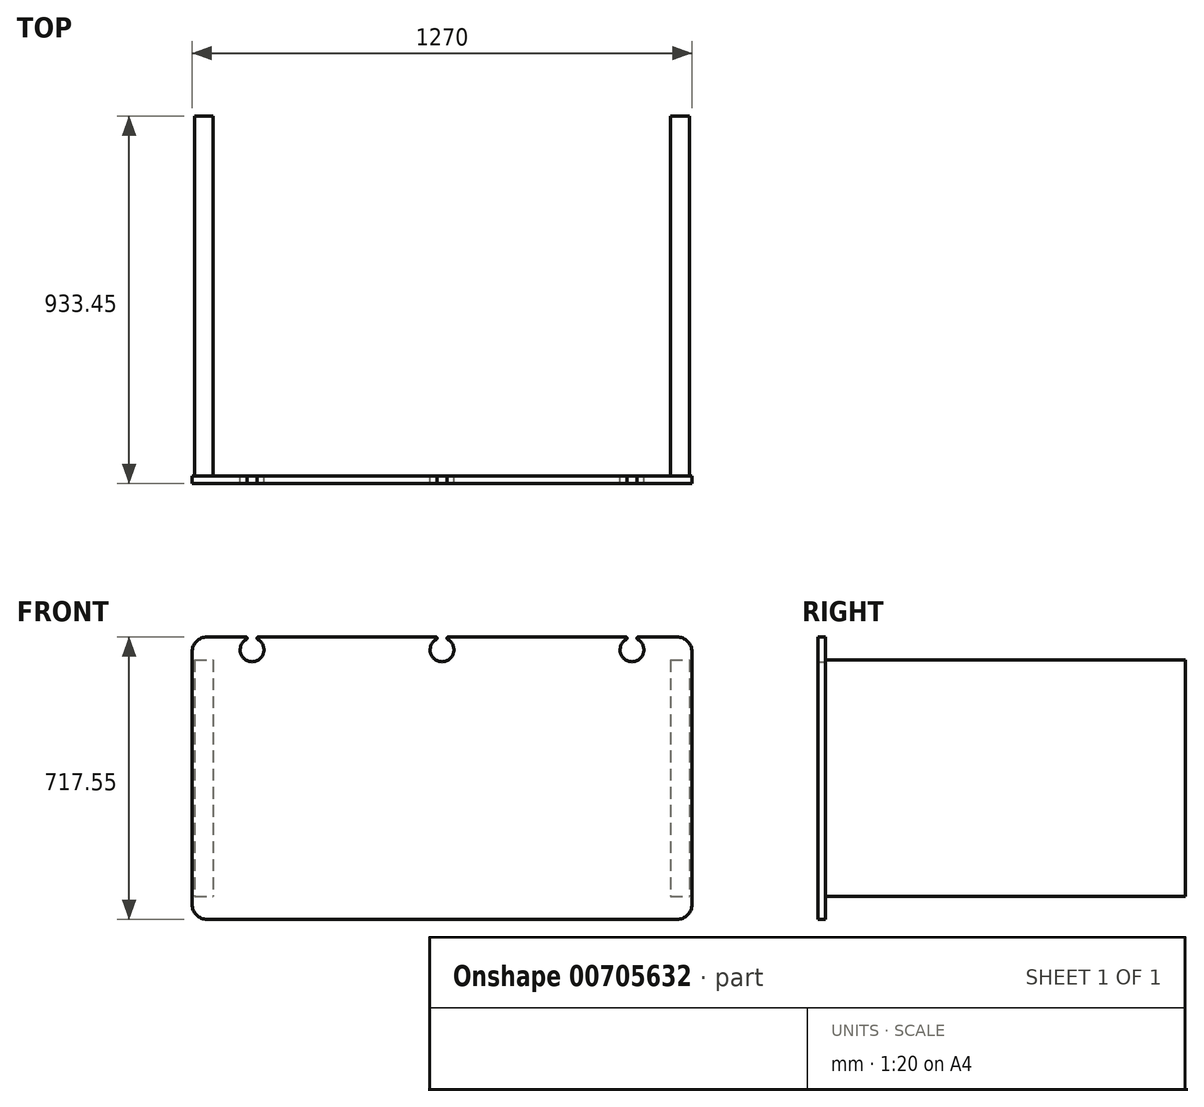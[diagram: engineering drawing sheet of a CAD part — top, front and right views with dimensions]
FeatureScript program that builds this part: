
annotation { "Feature Type Name" : "Feature", "Feature Type Description" : "" }
export const myFeature = defineFeature(function(context is Context, id is Id, definition is map)
    precondition{}
    {
        {
            var Q0;
            Q0=qCreatedBy(makeId("Front.planeOp"),FACE);
            var sketch = newSketch(context, id + "F0", { "sketchPlane" : qUnion([Q0])});
            skLineSegment(sketch, "E0.bottom", {"start": v(-67.46, 613.94) * mm, "end": v(-19.83, 613.94) * mm});
            skLineSegment(sketch, "E0.top", {"start": v(-67.46, 13.87) * mm, "end": v(-19.83, 13.87) * mm});
            skLineSegment(sketch, "E0.left", {"start": v(-67.46, 613.94) * mm, "end": v(-67.46, 13.87) * mm});
            skLineSegment(sketch, "E0.right", {"start": v(-19.83, 613.94) * mm, "end": v(-19.83, 13.87) * mm});
            skLineSegment(sketch, "E1.bottom", {"start": v(1142.22, 613.94) * mm, "end": v(1189.84, 613.94) * mm});
            skLineSegment(sketch, "E1.top", {"start": v(1142.22, 13.87) * mm, "end": v(1189.84, 13.87) * mm});
            skLineSegment(sketch, "E1.left", {"start": v(1142.22, 613.94) * mm, "end": v(1142.22, 13.87) * mm});
            skLineSegment(sketch, "E1.right", {"start": v(1189.84, 613.94) * mm, "end": v(1189.84, 13.87) * mm});
            skSolve(sketch);
        }
        {
            var Q0;
            Q0 = qSketchRegion(id + "F0", true);
            extrude(context, id + "F1", {"entities" : qUnion([Q0]), "depth" : 914.4 * mm, "offsetDistance" : 25.4 * mm});
        }
        {
            var Q0;
            Q0=makeQuery(id+"F1.opExtrude","CAP_FACE",FACE,{"disambiguationData":[OSD([sQuery(id+"F0.wireOp",EDGE,"E0.bottom"),sQuery(id+"F0.wireOp",EDGE,"E0.top"),sQuery(id+"F0.wireOp",EDGE,"E0.left"),sQuery(id+"F0.wireOp",EDGE,"E0.right")])],"isStart":false});
            var sketch = newSketch(context, id + "F2", { "sketchPlane" : qUnion([Q0])});
            skLineSegment(sketch, "E2.bottom", {"start": v(-35.7, 672.68) * mm, "end": v(62.72, 672.68) * mm});
            skLineSegment(sketch, "E2.top", {"start": v(-35.7, -44.87) * mm, "end": v(1158.1, -44.87) * mm});
            skLineSegment(sketch, "E2.left", {"start": v(-73.8, 634.58) * mm, "end": v(-73.8, -6.77) * mm});
            skLineSegment(sketch, "E2.right", {"start": v(1196.2, 634.58) * mm, "end": v(1196.2, -6.77) * mm});
            skPoint(sketch, "E3.visualSharp", {"position": v(-73.8, 672.68) * mm});
            skArc(sketch, "E3.filletArc", {"start": v(-35.7, 672.68) * mm, "mid": v(-62.65, 661.52) * mm, "end": v(-73.8, 634.58) * mm});
            skPoint(sketch, "E4.visualSharp", {"position": v(-73.8, -44.87) * mm});
            skArc(sketch, "E4.filletArc", {"start": v(-73.8, -6.77) * mm, "mid": v(-62.65, -33.71) * mm, "end": v(-35.7, -44.87) * mm});
            skPoint(sketch, "E5.visualSharp", {"position": v(1196.2, -44.87) * mm});
            skArc(sketch, "E5.filletArc", {"start": v(1158.1, -44.87) * mm, "mid": v(1185.03, -33.71) * mm, "end": v(1196.2, -6.77) * mm});
            skPoint(sketch, "E6.visualSharp", {"position": v(1196.2, 672.68) * mm});
            skArc(sketch, "E6.filletArc", {"start": v(1196.2, 634.58) * mm, "mid": v(1185.03, 661.52) * mm, "end": v(1158.1, 672.68) * mm});
            skLineSegment(sketch, "E7", {"start": v(561.2, 672.68) * mm, "end": v(561.2, -44.87) * mm, "construction": true});
            skLineSegment(sketch, "E8", {"start": v(1043.8, 672.68) * mm, "end": v(1043.8, 484.6) * mm, "construction": true});
            skArc(sketch, "E9", {"start": v(1029.43, 666.7) * mm, "mid": v(1043.8, 609.89) * mm, "end": v(1058.16, 666.7) * mm});
            skLineSegment(sketch, "E10.MirrorCS", {"start": v(1031.1, 669.5) * mm, "end": v(1031.1, 669.5) * mm});
            skLineSegment(sketch, "E11.trimOffspring", {"start": v(1059.67, 672.68) * mm, "end": v(1158.1, 672.68) * mm});
            skPoint(sketch, "E12.visualSharp", {"position": v(1031.1, 672.68) * mm});
            skArc(sketch, "E12.filletArc", {"start": v(1031.1, 669.5) * mm, "mid": v(1030.16, 671.75) * mm, "end": v(1027.92, 672.68) * mm});
            skPoint(sketch, "E13.visualSharp", {"position": v(1031.1, 667.54) * mm});
            skArc(sketch, "E13.filletArc", {"start": v(1029.43, 666.7) * mm, "mid": v(1030.64, 667.88) * mm, "end": v(1031.1, 669.5) * mm});
            skArc(sketch, "E14.MirrorCS", {"start": v(1058.16, 666.7) * mm, "mid": v(1056.94, 667.88) * mm, "end": v(1056.5, 669.5) * mm});
            skArc(sketch, "E15.MirrorCS", {"start": v(1056.5, 669.5) * mm, "mid": v(1057.42, 671.75) * mm, "end": v(1059.67, 672.68) * mm});
            skPoint(sketch, "E16.orphan", {"position": v(1056.5, 672.68) * mm});
            skPoint(sketch, "E17.orphan", {"position": v(1056.5, 667.54) * mm});
            skArc(sketch, "E18.MirrorCS", {"start": v(92.96, 666.7) * mm, "mid": v(78.6, 609.89) * mm, "end": v(64.23, 666.7) * mm});
            skArc(sketch, "E19.MirrorCS", {"start": v(91.3, 669.5) * mm, "mid": v(92.22, 671.75) * mm, "end": v(94.47, 672.68) * mm});
            skPoint(sketch, "E20.MirrorP", {"position": v(91.3, 667.54) * mm});
            skArc(sketch, "E21.MirrorCS", {"start": v(92.96, 666.7) * mm, "mid": v(91.74, 667.88) * mm, "end": v(91.3, 669.5) * mm});
            skPoint(sketch, "E22.MirrorP", {"position": v(65.9, 667.54) * mm});
            skArc(sketch, "E23.MirrorCS", {"start": v(65.9, 669.5) * mm, "mid": v(64.96, 671.75) * mm, "end": v(62.72, 672.68) * mm});
            skArc(sketch, "E24.MirrorCS", {"start": v(64.23, 666.7) * mm, "mid": v(65.44, 667.88) * mm, "end": v(65.9, 669.5) * mm});
            skLineSegment(sketch, "E25.trimOffspring", {"start": v(94.47, 672.68) * mm, "end": v(545.32, 672.68) * mm});
            skArc(sketch, "E26.MirrorCS", {"start": v(575.56, 666.7) * mm, "mid": v(561.2, 609.89) * mm, "end": v(546.83, 666.7) * mm});
            skArc(sketch, "E27.MirrorCS", {"start": v(573.9, 669.5) * mm, "mid": v(574.82, 671.75) * mm, "end": v(577.07, 672.68) * mm});
            skPoint(sketch, "E28.MirrorP", {"position": v(573.9, 749.05) * mm});
            skArc(sketch, "E29.MirrorCS", {"start": v(575.56, 666.7) * mm, "mid": v(574.34, 667.88) * mm, "end": v(573.9, 669.5) * mm});
            skArc(sketch, "E30.MirrorCS", {"start": v(548.5, 669.5) * mm, "mid": v(547.56, 671.75) * mm, "end": v(545.32, 672.68) * mm});
            skArc(sketch, "E31.MirrorCS", {"start": v(546.83, 666.7) * mm, "mid": v(548.04, 667.88) * mm, "end": v(548.5, 669.5) * mm});
            skLineSegment(sketch, "E32.trimOffspring", {"start": v(577.07, 672.68) * mm, "end": v(1027.92, 672.68) * mm});
            skSolve(sketch);
        }
        {
            var Q0;
            Q0=makeQuery(id+"F2.imprint","IMPRINT",FACE,{"disambiguationData":[TD([[makeQuery(id+"F2.imprint","IMPRINT",EDGE,{"derivedFrom":sQuery(id+"F2.wireOp",EDGE,"E2.bottom")}),-1.0]])]});
            var Q1;
            Q1=makeQuery(id+"F2.imprint","IMPRINT",FACE,{"disambiguationData":[TD([[makeQuery(id+"F2.imprint","IMPRINT",EDGE,{"derivedFrom":makeQuery(id+"F1.opExtrude","CAP_EDGE",EDGE,{"disambiguationData":[OSD([sQuery(id+"F0.wireOp",EDGE,"E0.bottom")])],"isStart":false})}),-1.0]])]});
            extrude(context, id + "F3", {"entities" : qUnion([Q0, Q1]), "operationType" : NewBodyOperationType.ADD, "depth" : 19.05 * mm, "offsetDistance" : 25.4 * mm});
        }
    });
